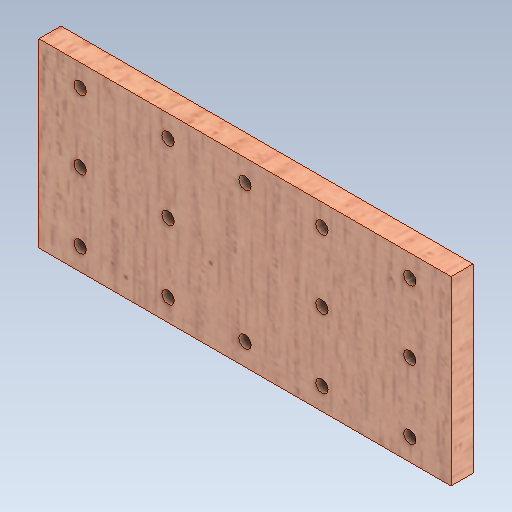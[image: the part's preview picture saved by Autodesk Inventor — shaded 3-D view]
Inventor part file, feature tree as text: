
AUTODESK INVENTOR PART (.ipt)
format: ipt  version: 2020 (Build 240168000, 168)  size: 304,640 bytes
history: native  units: mm
features: extrude x2, sketch x2
ambient origin geometry x8: Origin, YZ Plane, XZ Plane, XY Plane, X Axis, Y Axis, Z Axis, Center Point
bodies: Solid1 (feature_tree)
feature tree (4):
  extrude  "Extrusion1"  Depth=66.0mm
  extrude  "Extrusion4"  Depth=8.0mm
  sketch  "Sketch1"  dims[d0=150.0mm d1=66.0mm]
  sketch  "Sketch4"  dims[d2=8.0mm d3=0.0mm d19=4.5mm d20=15.0mm d21=8.0mm d22=8.0mm d23=32.0mm d24=15.0mm d26=32.0mm d27=0.0mm d28=0.0mm]
